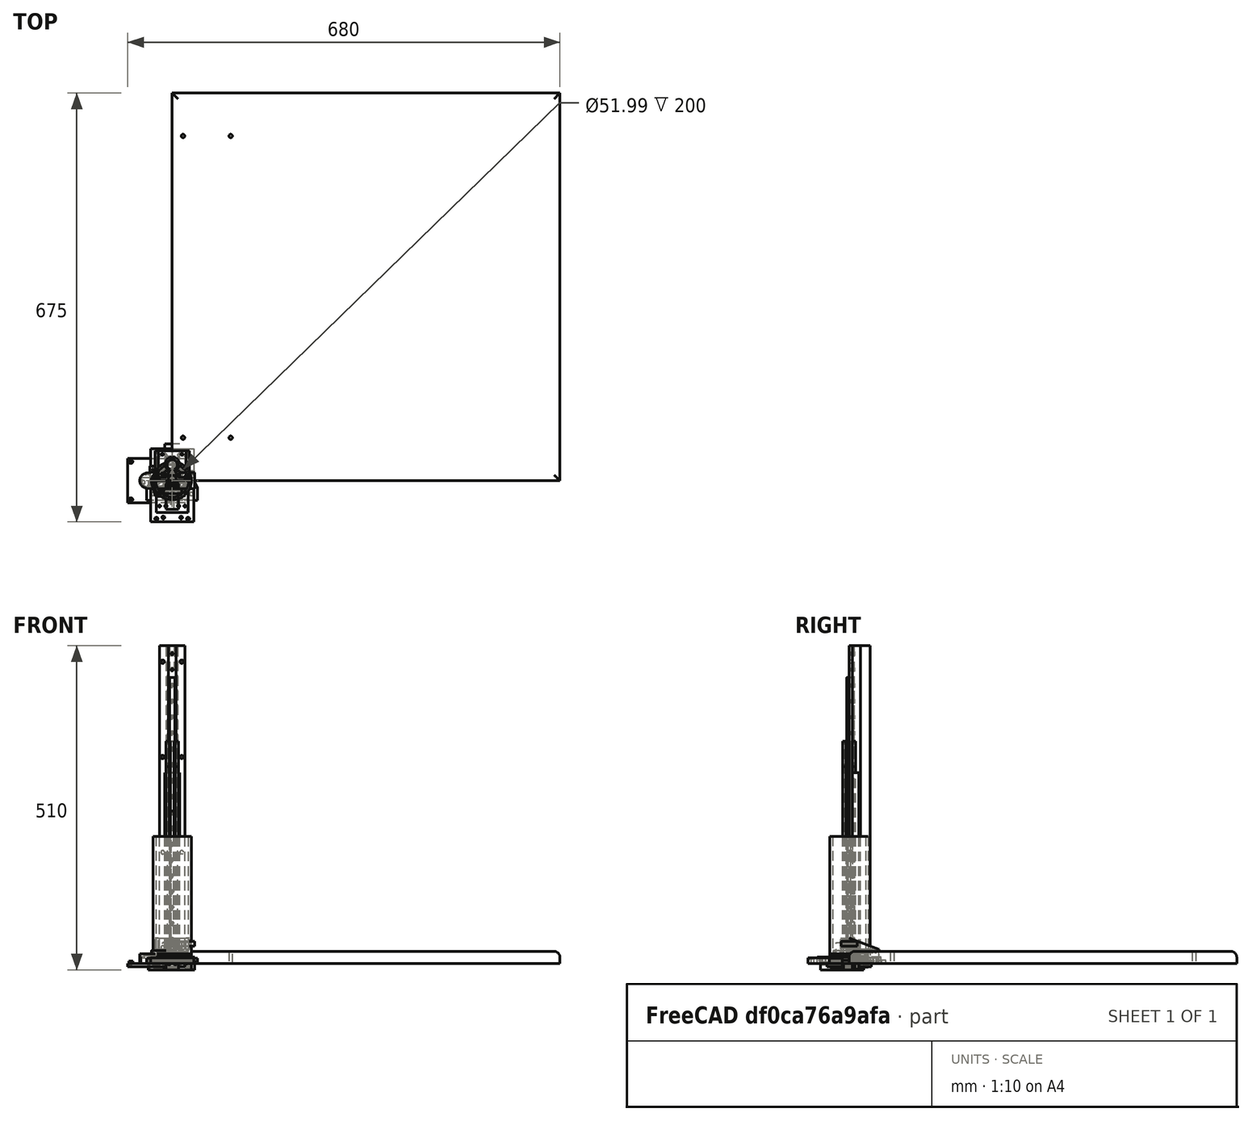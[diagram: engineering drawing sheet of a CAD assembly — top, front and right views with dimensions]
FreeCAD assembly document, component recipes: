
FREECAD ASSEMBLY — COMPONENT RECIPES ("MUSCLE_ROLLER_1V0")

This assembly document has 39 components, labeled P0..P38 below (a component is one placed body or linked part). 39 of them carry a construction recipe — the FreeCAD feature program that regenerates the part from scratch, quoted from this document or its linked companion documents; the rest are supplied as boundary geometry only. No exploded tour is included for this assembly.
NOTE — document 2 of 2 of this assembly tour. The two overview renders and the header above are repeated from document 1; the component sections below continue where the previous document stopped.
COMPONENT P30 — recipe-attached ("SHAFT_X", modeled in this document).
Construction recipe (the document's own serialized feature program — sketch geometry with constraints, then the solid features built on it; lengths are millimeters unless a unit is written):

FEATURE [PartDesign::CoordinateSystem] LCS_0075
  AttacherType = Attacher::AttachEngine3D
  MapMode = 2
  Support = -> [X_Axis082]
FEATURE [Sketcher::SketchObject] Sketch101
  FullyConstrained = true
  MapMode = 5
  Support = -> [XY_Plane082]
  sketch-geometry (8):
    g0: LineSegment StartX=-20 StartY=0 StartZ=0 EndX=20 EndY=0 EndZ=0
    g1: LineSegment StartX=20 StartY=0 StartZ=0 EndX=20 EndY=5 EndZ=0
    g2: LineSegment StartX=20 StartY=5 StartZ=0 EndX=9.25 EndY=5 EndZ=0
    g3: LineSegment StartX=9.25 StartY=5 StartZ=0 EndX=3.48712 EndY=17.8 EndZ=0
    g4: LineSegment StartX=-3.48712 StartY=17.8 StartZ=0 EndX=-9.25 EndY=5 EndZ=0
    g5: LineSegment StartX=-9.25 StartY=5 StartZ=0 EndX=-20 EndY=5 EndZ=0
    g6: LineSegment StartX=-20 StartY=5 StartZ=0 EndX=-20 EndY=0 EndZ=0
    g7: ArcOfCircle CenterX=-3.9e-15 CenterY=25 CenterZ=0 NormalX=0 NormalY=0 NormalZ=1 AngleXU=0 Radius=8 StartAngle=5.16342 EndAngle=10.5445
  constraints (22):
    c: PointOnObject(g0,g-1)
    c: Coincident(g0,g1)
    c: Vertical(g1)
    c: Coincident(g1,g2)
    c: Horizontal(g2)
    c: Coincident(g2,g3)
    c: Coincident(g4,g5)
    c: Coincident(g5,g6)
    c: Coincident(g6,g0)
    c: Vertical(g6)
    c: Horizontal(g5)
    c: Coincident(g7,g4)
    c: Coincident(g7,g3)
    c: Symmetric(g4,g3,g-2)
    c: Diameter(g7) = 16
    c: DistanceY(g-1,g7) = 25
    c: DistanceY(g-1,g4) = 17.8
    c: DistanceY(g6,g6) = 5
    c: Symmetric(g0,g0,g-2)
    c: DistanceX(g0,g0) = 40
    c: DistanceX(g4,g2) = 18.5
    c: Symmetric(g4,g2,g-2)
FEATURE [PartDesign::Pad] Pad064
  Direction = (1,1,1)
  Length = 500
  Length2 = 100
  Profile = -> Sketch101
  Refine = true
  Type = 0
FEATURE [Sketcher::SketchObject] Sketch111
  FullyConstrained = true
  MapMode = 5
  Placement = pos=(0,0,0) rot=(1,0,0;1.5708rad)
  Support = -> [XZ_Plane081]
  sketch-geometry (8):
    g0: Circle CenterX=-15 CenterY=25 CenterZ=0 NormalX=0 NormalY=0 NormalZ=1 AngleXU=0 Radius=2.75
    g1: Circle CenterX=15 CenterY=25 CenterZ=0 NormalX=0 NormalY=0 NormalZ=1 AngleXU=0 Radius=2.75
    g2: Circle CenterX=-15 CenterY=175 CenterZ=0 NormalX=0 NormalY=0 NormalZ=1 AngleXU=0 Radius=2.75
    g3: Circle CenterX=15 CenterY=175 CenterZ=0 NormalX=0 NormalY=0 NormalZ=1 AngleXU=0 Radius=2.75
    g4: Circle CenterX=-15 CenterY=325 CenterZ=0 NormalX=0 NormalY=0 NormalZ=1 AngleXU=0 Radius=2.75
    g5: Circle CenterX=15 CenterY=325 CenterZ=0 NormalX=0 NormalY=0 NormalZ=1 AngleXU=0 Radius=2.75
    g6: Circle CenterX=-15 CenterY=475 CenterZ=0 NormalX=0 NormalY=0 NormalZ=1 AngleXU=0 Radius=2.75
    g7: Circle CenterX=15 CenterY=475 CenterZ=0 NormalX=0 NormalY=0 NormalZ=1 AngleXU=0 Radius=2.75
  constraints (23):
    c: Diameter(g0) = 5.5
    c: Equal(g0,g2)
    c: Equal(g0,g4)
    c: Equal(g0,g6)
    c: Equal(g0,g7)
    c: Equal(g0,g5)
    c: Equal(g0,g3)
    c: Equal(g0,g1)
    c: Symmetric(g0,g1,g-2)
    c: Vertical(g0,g2)
    c: Vertical(g2,g4)
    c: Vertical(g4,g6)
    c: Horizontal(g7,g6)
    c: Vertical(g7,g5)
    c: Vertical(g5,g3)
    c: Vertical(g3,g1)
    c: Horizontal(g3,g2)
    c: Horizontal(g5,g4)
    c: DistanceY(g-1,g1) = 25
    c: DistanceY(g1,g3) = 150
    c: DistanceX(g0,g1) = 30
    c: DistanceY(g3,g5) = 150
    c: DistanceY(g5,g7) = 150
FEATURE [PartDesign::Pocket] Pocket036
  BaseFeature = -> Pad064
  Length = 5
  Length2 = 100
  Profile = -> Sketch111
  Refine = true
  Type = 1
FEATURE [PartDesign::Body] Body_13
  Group = -> [LCS_0075,Sketch101,Pad064,Sketch111,Pocket036]
  Origin = -> Origin082
  Tip = -> Pocket036
COMPONENT P31 — recipe-attached ("RAIL_Z_1V0", modeled in this document).
Construction recipe (the document's own serialized feature program — sketch geometry with constraints, then the solid features built on it; lengths are millimeters unless a unit is written):

FEATURE [PartDesign::CoordinateSystem] LCS_0090
  AttacherType = Attacher::AttachEngine3D
  MapMode = 2
  Support = -> [X_Axis098]
FEATURE [Sketcher::SketchObject] Sketch119
  FullyConstrained = true
  MapMode = 5
  Support = -> [XY_Plane098]
  sketch-geometry (12):
    g0: LineSegment StartX=-6 StartY=0 StartZ=0 EndX=-6 EndY=5 EndZ=0
    g1: LineSegment StartX=-6 StartY=5 StartZ=0 EndX=-5 EndY=5 EndZ=0
    g2: LineSegment StartX=-5 StartY=5 StartZ=0 EndX=-5 EndY=6 EndZ=0
    g3: LineSegment StartX=-5 StartY=6 StartZ=0 EndX=-6 EndY=6 EndZ=0
    g4: LineSegment StartX=-6 StartY=6 StartZ=0 EndX=-6 EndY=8 EndZ=0
    g5: LineSegment StartX=-6 StartY=8 StartZ=0 EndX=6 EndY=8 EndZ=0
    g6: LineSegment StartX=6 StartY=8 StartZ=0 EndX=6 EndY=6 EndZ=0
    g7: LineSegment StartX=6 StartY=6 StartZ=0 EndX=5 EndY=6 EndZ=0
    g8: LineSegment StartX=5 StartY=6 StartZ=0 EndX=5 EndY=5 EndZ=0
    g9: LineSegment StartX=5 StartY=5 StartZ=0 EndX=6 EndY=5 EndZ=0
    g10: LineSegment StartX=6 StartY=5 StartZ=0 EndX=6 EndY=0 EndZ=0
    g11: LineSegment StartX=6 StartY=0 StartZ=0 EndX=-6 EndY=0 EndZ=0
  constraints (34):
    c: PointOnObject(g0,g-1)
    c: Coincident(g0,g1)
    c: Horizontal(g1)
    c: Coincident(g1,g2)
    c: Coincident(g2,g3)
    c: Horizontal(g3)
    c: Coincident(g3,g4)
    c: Vertical(g4)
    c: Coincident(g4,g5)
    c: Coincident(g5,g6)
    c: Coincident(g6,g7)
    c: Horizontal(g7)
    c: Coincident(g7,g8)
    c: Coincident(g8,g9)
    c: Coincident(g9,g10)
    c: PointOnObject(g10,g-1)
    c: Vertical(g10)
    c: Coincident(g10,g11)
    c: Coincident(g11,g0)
    c: Vertical(g0)
    c: Vertical(g2)
    c: Vertical(g8)
    c: Horizontal(g9)
    c: DistanceY(g0,g0) = 5
    c: DistanceY(g2,g2) = 1
    c: DistanceY(g-1,g4) = 8
    c: Vertical(g0,g3)
    c: DistanceX(g11,g11) = 12
    c: DistanceX(g3,g3) = 1
    c: Vertical(g6)
    c: Symmetric(g4,g5,g-2)
    c: Vertical(g6,g9)
    c: Equal(g8,g2)
    c: Symmetric(g7,g2,g-2)
FEATURE [PartDesign::Pad] Pad073
  Direction = (1,1,1)
  Length = 500
  Length2 = 100
  Profile = -> Sketch119
  Refine = true
  Type = 0
FEATURE [Sketcher::SketchObject] Sketch120
  AttachmentOffset = pos=(0,0,-8) rot=(0,0,1;0rad)
  FullyConstrained = true
  MapMode = 5
  Placement = pos=(0,8,1.8e-15) rot=(1,0,0;1.5708rad)
  Support = -> [XZ_Plane097]
  sketch-geometry (1):
    g0: Circle CenterX=0 CenterY=12.5 CenterZ=0 NormalX=0 NormalY=0 NormalZ=1 AngleXU=0 Radius=1.75
  constraints (3):
    c: PointOnObject(g0,g-2)
    c: Diameter(g0) = 3.5
    c: DistanceY(g-1,g0) = 12.5
FEATURE [PartDesign::Hole] Hole001
  BaseFeature = -> Pad073
  Depth = 25
  DepthType = 1
  Diameter = 3.4
  DrillForDepth = false
  DrillPoint = 1
  DrillPointAngle = 118
  HoleCutCountersinkAngle = 90
  HoleCutCustomValues = false
  HoleCutDepth = 4.5
  HoleCutDiameter = 6.1
  HoleCutType = 1
  ModelActualThread = false
  Profile = -> Sketch120
  Refine = true
  Reversed = true
  Tapered = false
  TaperedAngle = 90
  ThreadAngle = 0
  ThreadClass = 0
  ThreadCutOffInner = 0
  ThreadCutOffOuter = 0
  ThreadDirection = 0
  ThreadFit = 0
  ThreadPitch = 0
  ThreadSize = 9
  ThreadType = 1
  Threaded = false
FEATURE [PartDesign::LinearPattern] LinearPattern
  BaseFeature = -> Hole001
  Direction = -> Sketch120 [V_Axis]
  Length = 475
  Occurrences = 20
  Originals = -> [Hole001]
  Refine = true
FEATURE [PartDesign::Body] Body_16
  Group = -> [LCS_0090,Sketch119,Pad073,Sketch120,Hole001,LinearPattern]
  Origin = -> Origin098
  Tip = -> LinearPattern
COMPONENT P32 — recipe-attached ("RAIL_X_1V0", modeled in this document).
Construction recipe (the document's own serialized feature program — sketch geometry with constraints, then the solid features built on it; lengths are millimeters unless a unit is written):

FEATURE [Sketcher::SketchObject] Sketch131
  AttachmentOffset = pos=(0,0,-8) rot=(0,0,1;0rad)
  FullyConstrained = true
  MapMode = 5
  Placement = pos=(0,8,1.8e-15) rot=(1,0,0;1.5708rad)
  Support = -> [XZ_Plane106]
  sketch-geometry (1):
    g0: Circle CenterX=0 CenterY=12.5 CenterZ=0 NormalX=0 NormalY=0 NormalZ=1 AngleXU=0 Radius=1.75
  constraints (3):
    c: PointOnObject(g0,g-2)
    c: Diameter(g0) = 3.5
    c: DistanceY(g-1,g0) = 12.5
FEATURE [Sketcher::SketchObject] Sketch132
  FullyConstrained = true
  MapMode = 5
  Support = -> [XY_Plane107]
  sketch-geometry (12):
    g0: LineSegment StartX=-6 StartY=0 StartZ=0 EndX=-6 EndY=5 EndZ=0
    g1: LineSegment StartX=-6 StartY=5 StartZ=0 EndX=-5 EndY=5 EndZ=0
    g2: LineSegment StartX=-5 StartY=5 StartZ=0 EndX=-5 EndY=6 EndZ=0
    g3: LineSegment StartX=-5 StartY=6 StartZ=0 EndX=-6 EndY=6 EndZ=0
    g4: LineSegment StartX=-6 StartY=6 StartZ=0 EndX=-6 EndY=8 EndZ=0
    g5: LineSegment StartX=-6 StartY=8 StartZ=0 EndX=6 EndY=8 EndZ=0
    g6: LineSegment StartX=6 StartY=8 StartZ=0 EndX=6 EndY=6 EndZ=0
    g7: LineSegment StartX=6 StartY=6 StartZ=0 EndX=5 EndY=6 EndZ=0
    g8: LineSegment StartX=5 StartY=6 StartZ=0 EndX=5 EndY=5 EndZ=0
    g9: LineSegment StartX=5 StartY=5 StartZ=0 EndX=6 EndY=5 EndZ=0
    g10: LineSegment StartX=6 StartY=5 StartZ=0 EndX=6 EndY=0 EndZ=0
    g11: LineSegment StartX=6 StartY=0 StartZ=0 EndX=-6 EndY=0 EndZ=0
  constraints (34):
    c: PointOnObject(g0,g-1)
    c: Coincident(g0,g1)
    c: Horizontal(g1)
    c: Coincident(g1,g2)
    c: Coincident(g2,g3)
    c: Horizontal(g3)
    c: Coincident(g3,g4)
    c: Vertical(g4)
    c: Coincident(g4,g5)
    c: Coincident(g5,g6)
    c: Coincident(g6,g7)
    c: Horizontal(g7)
    c: Coincident(g7,g8)
    c: Coincident(g8,g9)
    c: Coincident(g9,g10)
    c: PointOnObject(g10,g-1)
    c: Vertical(g10)
    c: Coincident(g10,g11)
    c: Coincident(g11,g0)
    c: Vertical(g0)
    c: Vertical(g2)
    c: Vertical(g8)
    c: Horizontal(g9)
    c: DistanceY(g0,g0) = 5
    c: DistanceY(g2,g2) = 1
    c: DistanceY(g-1,g4) = 8
    c: Vertical(g0,g3)
    c: DistanceX(g11,g11) = 12
    c: DistanceX(g3,g3) = 1
    c: Vertical(g6)
    c: Symmetric(g4,g5,g-2)
    c: Vertical(g6,g9)
    c: Equal(g8,g2)
    c: Symmetric(g7,g2,g-2)
FEATURE [PartDesign::Pad] Pad078
  Direction = (1,1,1)
  Length = 500
  Length2 = 100
  Profile = -> Sketch132
  Refine = true
  Type = 0
FEATURE [PartDesign::Hole] Hole002
  BaseFeature = -> Pad078
  Depth = 25
  DepthType = 1
  Diameter = 3.4
  DrillForDepth = false
  DrillPoint = 1
  DrillPointAngle = 118
  HoleCutCountersinkAngle = 90
  HoleCutCustomValues = false
  HoleCutDepth = 4.5
  HoleCutDiameter = 6.1
  HoleCutType = 1
  ModelActualThread = false
  Profile = -> Sketch131
  Refine = true
  Reversed = true
  Tapered = false
  TaperedAngle = 90
  ThreadAngle = 0
  ThreadClass = 0
  ThreadCutOffInner = 0
  ThreadCutOffOuter = 0
  ThreadDirection = 0
  ThreadFit = 0
  ThreadPitch = 0
  ThreadSize = 9
  ThreadType = 1
  Threaded = false
FEATURE [PartDesign::LinearPattern] LinearPattern001
  BaseFeature = -> Hole002
  Direction = -> Sketch131 [V_Axis]
  Length = 475
  Occurrences = 20
  Originals = -> [Hole002]
  Refine = true
FEATURE [PartDesign::CoordinateSystem] LCS_0100
  AttacherType = Attacher::AttachEngine3D
  MapMode = 2
  Support = -> [X_Axis107]
FEATURE [PartDesign::Body] Body_027
  Group = -> [LCS_0100,Sketch132,Pad078,Sketch131,Hole002,LinearPattern001]
  Origin = -> Origin107
  Tip = -> LinearPattern001
COMPONENT P33 — recipe-attached ("ROLLER_1V0", modeled in this document).
Construction recipe (the document's own serialized feature program — sketch geometry with constraints, then the solid features built on it; lengths are millimeters unless a unit is written):

FEATURE [PartDesign::CoordinateSystem] LCS_0001
  AttacherType = Attacher::AttachEngine3D
  MapMode = 2
  Support = -> [X_Axis002]
FEATURE [Sketcher::SketchObject] Sketch
  FullyConstrained = true
  MapMode = 5
  Support = -> [XY_Plane002]
  expr: Constraints[2] = Variables.rollerOD
  expr: Constraints[3] = Variables.rollerID
  sketch-geometry (2):
    g0: Circle CenterX=0 CenterY=0 CenterZ=0 NormalX=0 NormalY=0 NormalZ=1 AngleXU=0 Radius=25.9969
    g1: Circle CenterX=0 CenterY=0 CenterZ=0 NormalX=0 NormalY=0 NormalZ=1 AngleXU=0 Radius=30.1625
  constraints (4):
    c: Coincident(g0,g-1)
    c: Coincident(g1,g0)
    c: Diameter(g1) = 60.325
    c: Diameter(g0) = 51.9938
FEATURE [PartDesign::Pad] Pad
  Direction = (1,1,1)
  Length = 200
  Length2 = 100
  Profile = -> Sketch
  Refine = true
  Type = 0
FEATURE [PartDesign::Body] Body
  Group = -> [LCS_0001,Sketch,Pad]
  Origin = -> Origin002
  Tip = -> Pad
COMPONENT P34 — recipe-attached ("ROLLER_BRACK_1V0", modeled in this document).
Construction recipe (the document's own serialized feature program — sketch geometry with constraints, then the solid features built on it; lengths are millimeters unless a unit is written):

FEATURE [PartDesign::CoordinateSystem] LCS_0050
  AttacherType = Attacher::AttachEngine3D
  MapMode = 2
  Support = -> [X_Axis056]
FEATURE [Sketcher::SketchObject] Sketch064
  FullyConstrained = true
  MapMode = 5
  Support = -> [XY_Plane056]
  sketch-geometry (9):
    g0: Circle CenterX=0 CenterY=0 CenterZ=0 NormalX=0 NormalY=0 NormalZ=1 AngleXU=0 Radius=5.25
    g1: LineSegment StartX=35 StartY=15 StartZ=0 EndX=-35 EndY=15 EndZ=0
    g2: LineSegment StartX=-35 StartY=15 StartZ=0 EndX=-35 EndY=5 EndZ=0
    g3: LineSegment StartX=-35 StartY=5 StartZ=0 EndX=-9 EndY=5 EndZ=0
    g4: LineSegment StartX=-9 StartY=5 StartZ=0 EndX=-9 EndY=0 EndZ=0
    g5: LineSegment StartX=9 StartY=0 StartZ=0 EndX=9 EndY=5 EndZ=0
    g6: LineSegment StartX=9 StartY=5 StartZ=0 EndX=35 EndY=5 EndZ=0
    g7: LineSegment StartX=35 StartY=5 StartZ=0 EndX=35 EndY=15 EndZ=0
    g8: ArcOfCircle CenterX=0 CenterY=0 CenterZ=0 NormalX=0 NormalY=0 NormalZ=1 AngleXU=0 Radius=9 StartAngle=3.14159 EndAngle=6.28319
  constraints (25):
    c: Coincident(g0,g-1)
    c: Diameter(g0) = 10.5
    c: Coincident(g1,g2)
    c: Vertical(g2)
    c: Coincident(g2,g3)
    c: Horizontal(g3)
    c: Coincident(g3,g4)
    c: PointOnObject(g4,g-1)
    c: PointOnObject(g5,g-1)
    c: Coincident(g5,g6)
    c: Horizontal(g6)
    c: Coincident(g6,g7)
    c: Coincident(g7,g1)
    c: Vertical(g7)
    c: DistanceY(g7,g7) = 10
    c: Coincident(g8,g0)
    c: Coincident(g8,g4)
    c: Coincident(g8,g5)
    c: Horizontal(g5,g3)
    c: Vertical(g5)
    c: Diameter(g8) = 18
    c: Vertical(g4)
    c: DistanceY(g5,g5) = 5
    c: DistanceX(g1,g1) = 70
    c: Symmetric(g1,g1,g-2)
FEATURE [PartDesign::Pad] Pad044
  Direction = (1,1,1)
  Length = 18
  Length2 = 100
  Midplane = true
  Profile = -> Sketch064
  Type = 0
FEATURE [Sketcher::SketchObject] Sketch065
  FullyConstrained = true
  MapMode = 5
  Placement = pos=(0,0,0) rot=(1,0,0;1.5708rad)
  Support = -> [XZ_Plane056]
  sketch-geometry (2):
    g0: Circle CenterX=-25 CenterY=0 CenterZ=0 NormalX=0 NormalY=0 NormalZ=1 AngleXU=0 Radius=2.75
    g1: Circle CenterX=25 CenterY=0 CenterZ=0 NormalX=0 NormalY=0 NormalZ=1 AngleXU=0 Radius=2.75
  constraints (5):
    c: PointOnObject(g1,g-1)
    c: Diameter(g1) = 5.5
    c: Equal(g1,g0)
    c: DistanceX(g0,g1) = 50
    c: Symmetric(g0,g1,g-2)
FEATURE [PartDesign::Pocket] Pocket016
  BaseFeature = -> Pad044
  Length = 5
  Length2 = 100
  Profile = -> Sketch065
  Type = 1
FEATURE [Sketcher::SketchObject] Sketch066
  AttachmentOffset = pos=(0,0,-15) rot=(0,0,1;0rad)
  FullyConstrained = true
  MapMode = 5
  Placement = pos=(0,15,3.3e-15) rot=(1,0,0;1.5708rad)
  Support = -> [XZ_Plane056]
  sketch-geometry (2):
    g0: Circle CenterX=-25 CenterY=0 CenterZ=0 NormalX=0 NormalY=0 NormalZ=1 AngleXU=0 Radius=6.5
    g1: Circle CenterX=25 CenterY=0 CenterZ=0 NormalX=0 NormalY=0 NormalZ=1 AngleXU=0 Radius=6.5
  constraints (5):
    c: PointOnObject(g0,g-1)
    c: Diameter(g1) = 13
    c: Equal(g1,g0)
    c: Symmetric(g1,g0,g-2)
    c: DistanceX(g0,g1) = 50
FEATURE [PartDesign::Pocket] Pocket017
  BaseFeature = -> Pocket016
  Length = 2
  Length2 = 100
  Profile = -> Sketch066
  Reversed = true
  Type = 0
FEATURE [Sketcher::SketchObject] Sketch067
  AttachmentOffset = pos=(0,0,-9) rot=(0,0,1;0rad)
  FullyConstrained = true
  MapMode = 5
  Placement = pos=(0,0,-9) rot=(0,0,1;0rad)
  Support = -> [XY_Plane056]
  sketch-geometry (1):
    g0: Circle CenterX=0 CenterY=0 CenterZ=0 NormalX=0 NormalY=0 NormalZ=1 AngleXU=0 Radius=9
  constraints (2):
    c: Coincident(g0,g-1)
    c: Diameter(g0) = 18
FEATURE [PartDesign::Pad] Pad045
  BaseFeature = -> Pocket017
  Direction = (1,1,1)
  Length = 2
  Length2 = 100
  Profile = -> Sketch067
  Type = 0
FEATURE [Sketcher::SketchObject] Sketch068
  AttachmentOffset = pos=(0,0,-5) rot=(0,0,1;0rad)
  FullyConstrained = true
  MapMode = 5
  Placement = pos=(0,5,1.1e-15) rot=(1,0,0;1.5708rad)
  Support = -> [XZ_Plane056]
  sketch-geometry (8):
    g0: LineSegment StartX=-29.8625 StartY=-4.8625 StartZ=0 EndX=-20.1375 EndY=-4.8625 EndZ=0
    g1: LineSegment StartX=-20.1375 StartY=-4.8625 StartZ=0 EndX=-20.1375 EndY=4.8625 EndZ=0
    g2: LineSegment StartX=-20.1375 StartY=4.8625 StartZ=0 EndX=-29.8625 EndY=4.8625 EndZ=0
    g3: LineSegment StartX=-29.8625 StartY=4.8625 StartZ=0 EndX=-29.8625 EndY=-4.8625 EndZ=0
    g4: LineSegment StartX=20.1375 StartY=-4.8625 StartZ=0 EndX=29.8625 EndY=-4.8625 EndZ=0
    g5: LineSegment StartX=29.8625 StartY=-4.8625 StartZ=0 EndX=29.8625 EndY=4.8625 EndZ=0
    g6: LineSegment StartX=29.8625 StartY=4.8625 StartZ=0 EndX=20.1375 EndY=4.8625 EndZ=0
    g7: LineSegment StartX=20.1375 StartY=4.8625 StartZ=0 EndX=20.1375 EndY=-4.8625 EndZ=0
  constraints (22):
    c: Coincident(g0,g1)
    c: Coincident(g1,g2)
    c: Coincident(g2,g3)
    c: Coincident(g3,g0)
    c: Horizontal(g0)
    c: Horizontal(g2)
    c: Vertical(g1)
    c: Coincident(g4,g5)
    c: Coincident(g5,g6)
    c: Coincident(g6,g7)
    c: Coincident(g7,g4)
    c: Horizontal(g4)
    c: Horizontal(g6)
    c: Vertical(g5)
    c: Vertical(g7)
    c: Equal(g2,g3)
    c: Equal(g3,g6)
    c: Equal(g6,g7)
    c: DistanceX(g2,g2) = 9.725
    c: Symmetric(g2,g0,g-1)
    c: Symmetric(g0,g4,g-2)
    c: DistanceX(g0,g4) = 40.275
FEATURE [PartDesign::Pocket] Pocket018
  BaseFeature = -> Pad045
  Length = 4
  Length2 = 100
  Profile = -> Sketch068
  Type = 0
FEATURE [PartDesign::Body] Body_6
  Group = -> [LCS_0050,Sketch064,Pad044,Sketch065,Pocket016,Sketch066,Pocket017,Sketch067,Pad045,Sketch068,Pocket018]
  Origin = -> Origin056
  Tip = -> Pocket018
COMPONENT P35 — recipe-attached ("ROLLER_CAP_1V0", modeled in this document).
Construction recipe (the document's own serialized feature program — sketch geometry with constraints, then the solid features built on it; lengths are millimeters unless a unit is written):

FEATURE [PartDesign::CoordinateSystem] LCS_0003
  AttacherType = Attacher::AttachEngine3D
  MapMode = 2
  Support = -> [X_Axis004]
FEATURE [Sketcher::SketchObject] Sketch001
  FullyConstrained = true
  MapMode = 5
  Support = -> [XY_Plane004]
  expr: Constraints[1] = Variables.rollerID - 0.2
  sketch-geometry (1):
    g0: Circle CenterX=0 CenterY=0 CenterZ=0 NormalX=0 NormalY=0 NormalZ=1 AngleXU=0 Radius=25.8969
  constraints (2):
    c: Coincident(g0,g-1)
    c: Diameter(g0) = 51.7938
FEATURE [PartDesign::Pad] Pad001
  Direction = (1,1,1)
  Length = 15
  Length2 = 100
  Profile = -> Sketch001
  Refine = true
  Type = 0
FEATURE [Sketcher::SketchObject] Sketch002
  AttachmentOffset = pos=(0,0,15) rot=(0,0,1;0rad)
  FullyConstrained = true
  MapMode = 5
  Placement = pos=(0,0,15) rot=(0,0,1;0rad)
  Support = -> [XY_Plane004]
  sketch-geometry (1):
    g0: Circle CenterX=0 CenterY=0 CenterZ=0 NormalX=0 NormalY=0 NormalZ=1 AngleXU=0 Radius=15.1
  constraints (2):
    c: Coincident(g0,g-1)
    c: Diameter(g0) = 30.2
FEATURE [Sketcher::SketchObject] Sketch003
  FullyConstrained = true
  MapMode = 5
  Support = -> [XY_Plane004]
  sketch-geometry (1):
    g0: Circle CenterX=0 CenterY=0 CenterZ=0 NormalX=0 NormalY=0 NormalZ=1 AngleXU=0 Radius=13
  constraints (2):
    c: Coincident(g0,g-1)
    c: Diameter(g0) = 26
FEATURE [Sketcher::SketchObject] Sketch004
  AttachmentOffset = pos=(0,0,15) rot=(0,0,1;0rad)
  FullyConstrained = true
  MapMode = 5
  Placement = pos=(0,0,15) rot=(0,0,1;0rad)
  Support = -> [XY_Plane004]
  expr: Constraints[1] = Variables.rollerOD
  sketch-geometry (1):
    g0: Circle CenterX=0 CenterY=0 CenterZ=0 NormalX=0 NormalY=0 NormalZ=1 AngleXU=0 Radius=30.1625
  constraints (2):
    c: Coincident(g0,g-1)
    c: Diameter(g0) = 60.325
FEATURE [PartDesign::Pad] Pad002
  BaseFeature = -> Pad001
  Direction = (1,1,1)
  Length = 3
  Length2 = 100
  Profile = -> Sketch004
  Refine = true
  Reversed = true
  Type = 0
FEATURE [PartDesign::Pocket] Pocket
  BaseFeature = -> Pad002
  Length = 9
  Length2 = 100
  Profile = -> Sketch002
  Refine = true
  Type = 0
FEATURE [PartDesign::Pocket] Pocket001
  BaseFeature = -> Pocket
  Length = 5
  Length2 = 100
  Profile = -> Sketch003
  Refine = true
  Reversed = true
  Type = 1
FEATURE [PartDesign::Body] Body_2
  Group = -> [LCS_0003,Sketch001,Pad001,Sketch002,Sketch003,Sketch004,Pad002,Pocket,Pocket001]
  Origin = -> Origin004
  Tip = -> Pocket001
COMPONENT P36 — recipe-attached ("SHAFT_1V0", modeled in this document).
Construction recipe (the document's own serialized feature program — sketch geometry with constraints, then the solid features built on it; lengths are millimeters unless a unit is written):

FEATURE [PartDesign::CoordinateSystem] LCS_0005
  AttacherType = Attacher::AttachEngine3D
  MapMode = 2
  Support = -> [X_Axis006]
FEATURE [Sketcher::SketchObject] Sketch005
  FullyConstrained = true
  MapMode = 5
  Support = -> [XY_Plane006]
  sketch-geometry (1):
    g0: Circle CenterX=0 CenterY=0 CenterZ=0 NormalX=0 NormalY=0 NormalZ=1 AngleXU=0 Radius=5
  constraints (2):
    c: Coincident(g0,g-1)
    c: Diameter(g0) = 10
FEATURE [PartDesign::Pad] Pad003
  Direction = (1,1,1)
  Length = 240
  Length2 = 100
  Profile = -> Sketch005
  Refine = true
  Type = 0
FEATURE [PartDesign::Body] Body_3
  Group = -> [LCS_0005,Sketch005,Pad003]
  Origin = -> Origin006
  Tip = -> Pad003
COMPONENT P37 — recipe-attached ("X_MAG_BRACK_1V0", modeled in this document).
Construction recipe (the document's own serialized feature program — sketch geometry with constraints, then the solid features built on it; lengths are millimeters unless a unit is written):

FEATURE [PartDesign::CoordinateSystem] LCS_0126
  AttacherType = Attacher::AttachEngine3D
  MapMode = 2
  Support = -> [X_Axis138]
FEATURE [Sketcher::SketchObject] Sketch164
  FullyConstrained = true
  MapMode = 5
  Support = -> [XY_Plane138]
  sketch-geometry (6):
    g0: LineSegment StartX=0 StartY=-5 StartZ=0 EndX=-50 EndY=-5 EndZ=0
    g1: LineSegment StartX=-50 StartY=-5 StartZ=0 EndX=-50 EndY=5 EndZ=0
    g2: LineSegment StartX=-50 StartY=5 StartZ=0 EndX=-7.1e-15 EndY=5 EndZ=0
    g3: LineSegment StartX=-7.1e-15 StartY=5 StartZ=0 EndX=0 EndY=-5 EndZ=0
    g4: Circle CenterX=-5 CenterY=0 CenterZ=0 NormalX=0 NormalY=0 NormalZ=1 AngleXU=0 Radius=1.75
    g5: Circle CenterX=-25 CenterY=0 CenterZ=0 NormalX=0 NormalY=0 NormalZ=1 AngleXU=0 Radius=1.75
  constraints (17):
    c: Coincident(g0,g1)
    c: Coincident(g1,g2)
    c: Coincident(g2,g3)
    c: Coincident(g3,g0)
    c: Horizontal(g0)
    c: Horizontal(g2)
    c: Vertical(g1)
    c: PointOnObject(g0,g-2)
    c: PointOnObject(g4,g-1)
    c: PointOnObject(g5,g-1)
    c: DistanceX(g5,g4) = 20
    c: Equal(g5,g4)
    c: Diameter(g5) = 3.5
    c: DistanceX(g4,g2) = 5
    c: Symmetric(g0,g2,g-1)
    c: DistanceY(g3,g3) = 10
    c: DistanceX(g2,g2) = 50
FEATURE [PartDesign::Pad] Pad093
  Direction = (1,1,1)
  Length = 10
  Length2 = 100
  Profile = -> Sketch164
  Type = 0
FEATURE [Sketcher::SketchObject] Sketch165
  AttachmentOffset = pos=(0,0,10) rot=(0,0,1;0rad)
  FullyConstrained = true
  MapMode = 5
  Placement = pos=(0,0,10) rot=(0,0,1;0rad)
  Support = -> [XY_Plane138]
  sketch-geometry (4):
    g0: ArcOfCircle CenterX=-45.35 CenterY=-12.5 CenterZ=0 NormalX=0 NormalY=0 NormalZ=1 AngleXU=0 Radius=2.65 StartAngle=3.14159 EndAngle=6.28319
    g1: ArcOfCircle CenterX=-45.35 CenterY=-2.5 CenterZ=0 NormalX=0 NormalY=0 NormalZ=1 AngleXU=0 Radius=2.65 StartAngle=1e-16 EndAngle=3.14159
    g2: LineSegment StartX=-42.7 StartY=-12.5 StartZ=0 EndX=-42.7 EndY=-2.5 EndZ=0
    g3: LineSegment StartX=-48 StartY=-12.5 StartZ=0 EndX=-48 EndY=-2.5 EndZ=0
  constraints (10):
    c: Tangent(g0,g3) = 1.5708
    c: Tangent(g0,g2) = -1.5708
    c: Tangent(g2,g1) = -1.5708
    c: Tangent(g3,g1) = 1.5708
    c: Vertical(g2)
    c: Equal(g0,g1)
    c: Diameter(g0) = 5.3
    c: DistanceY(g2,g2) = 10
    c: DistanceX(g0,g-1) = 48
    c: DistanceY(g1,g-1) = 2.5
FEATURE [PartDesign::Pocket] Pocket062
  BaseFeature = -> Pad093
  Length = 2
  Length2 = 100
  Profile = -> Sketch165
  Type = 0
FEATURE [PartDesign::Body] Body_27
  Group = -> [LCS_0126,Sketch164,Pad093,Sketch165,Pocket062]
  Origin = -> Origin138
  Tip = -> Pocket062
COMPONENT P38 — recipe-attached ("Z_MAG_BRACK_1V0", modeled in this document).
Construction recipe (the document's own serialized feature program — sketch geometry with constraints, then the solid features built on it; lengths are millimeters unless a unit is written):

FEATURE [PartDesign::CoordinateSystem] LCS_0124
  AttacherType = Attacher::AttachEngine3D
  MapMode = 2
  Support = -> [X_Axis136]
FEATURE [Sketcher::SketchObject] Sketch162
  FullyConstrained = true
  MapMode = 5
  Support = -> [XY_Plane136]
  expr: Constraints[22] = Variables.zHomeL
  sketch-geometry (8):
    g0: LineSegment StartX=0 StartY=0 StartZ=0 EndX=-9 EndY=0 EndZ=0
    g1: LineSegment StartX=-9 StartY=0 StartZ=0 EndX=-17 EndY=4.5 EndZ=0
    g2: LineSegment StartX=-17 StartY=4.5 StartZ=0 EndX=-17 EndY=13.5 EndZ=0
    g3: LineSegment StartX=-17 StartY=13.5 StartZ=0 EndX=-9 EndY=20 EndZ=0
    g4: LineSegment StartX=-9 StartY=20 StartZ=0 EndX=0 EndY=20 EndZ=0
    g5: LineSegment StartX=0 StartY=20 StartZ=0 EndX=0 EndY=0 EndZ=0
    g6: Circle CenterX=-4 CenterY=15 CenterZ=0 NormalX=0 NormalY=0 NormalZ=1 AngleXU=0 Radius=1.65
    g7: Circle CenterX=-4 CenterY=5 CenterZ=0 NormalX=0 NormalY=0 NormalZ=1 AngleXU=0 Radius=1.65
  constraints (23):
    c: Coincident(g-1,g0)
    c: PointOnObject(g0,g-1)
    c: Coincident(g0,g1)
    c: Coincident(g1,g2)
    c: Vertical(g2)
    c: Coincident(g2,g3)
    c: Coincident(g3,g4)
    c: PointOnObject(g4,g-2)
    c: Horizontal(g4)
    c: Coincident(g4,g5)
    c: Coincident(g5,g0)
    c: Equal(g0,g4)
    c: Equal(g7,g6)
    c: Diameter(g7) = 3.3
    c: DistanceX(g0,g0) = 9
    c: DistanceX(g7,g0) = 4
    c: DistanceY(g7,g6) = 10
    c: Vertical(g6,g7)
    c: DistanceY(g0,g7) = 5
    c: DistanceY(g6,g4) = 5
    c: DistanceY(g2,g2) = 9
    c: DistanceY(g-1,g1) = 4.5
    c: DistanceX(g1,g0) = 17
FEATURE [PartDesign::Pad] Pad092
  Direction = (1,1,1)
  Length = 3
  Length2 = 100
  Profile = -> Sketch162
  Type = 0
FEATURE [Sketcher::SketchObject] Sketch163
  AttachmentOffset = pos=(0,0,-17) rot=(0,0,1;0rad)
  FullyConstrained = true
  MapMode = 5
  Placement = pos=(-17,3.8e-15,-3.8e-15) rot=(0.57735,0.57735,0.57735;2.0944rad)
  Support = -> [YZ_Plane136]
  expr: .AttachmentOffset.Base.z = -Variables.zHomeL
  sketch-geometry (1):
    g0: Circle CenterX=9 CenterY=1.5 CenterZ=0 NormalX=0 NormalY=0 NormalZ=1 AngleXU=0 Radius=2.6376
  constraints (3):
    c: Diameter(g0) = 5.2752
    c: DistanceX(g-1,g0) = 9
    c: DistanceY(g-1,g0) = 1.5
FEATURE [PartDesign::Pocket] Pocket061
  BaseFeature = -> Pad092
  Length = 2
  Length2 = 100
  Profile = -> Sketch163
  Reversed = true
  Type = 0
FEATURE [PartDesign::Body] Body_26
  Group = -> [LCS_0124,Sketch162,Pad092,Sketch163,Pocket061]
  Origin = -> Origin136
  Tip = -> Pocket061
PROVENANCE & LICENSES
A FreeCAD (.FCStd) document from a public repository crawl; recipes are the document's own serialized feature recipes (and, for linked parts, companion documents' recipes).
License: as declared in the source repository (recorded in the dataset sidecar).
